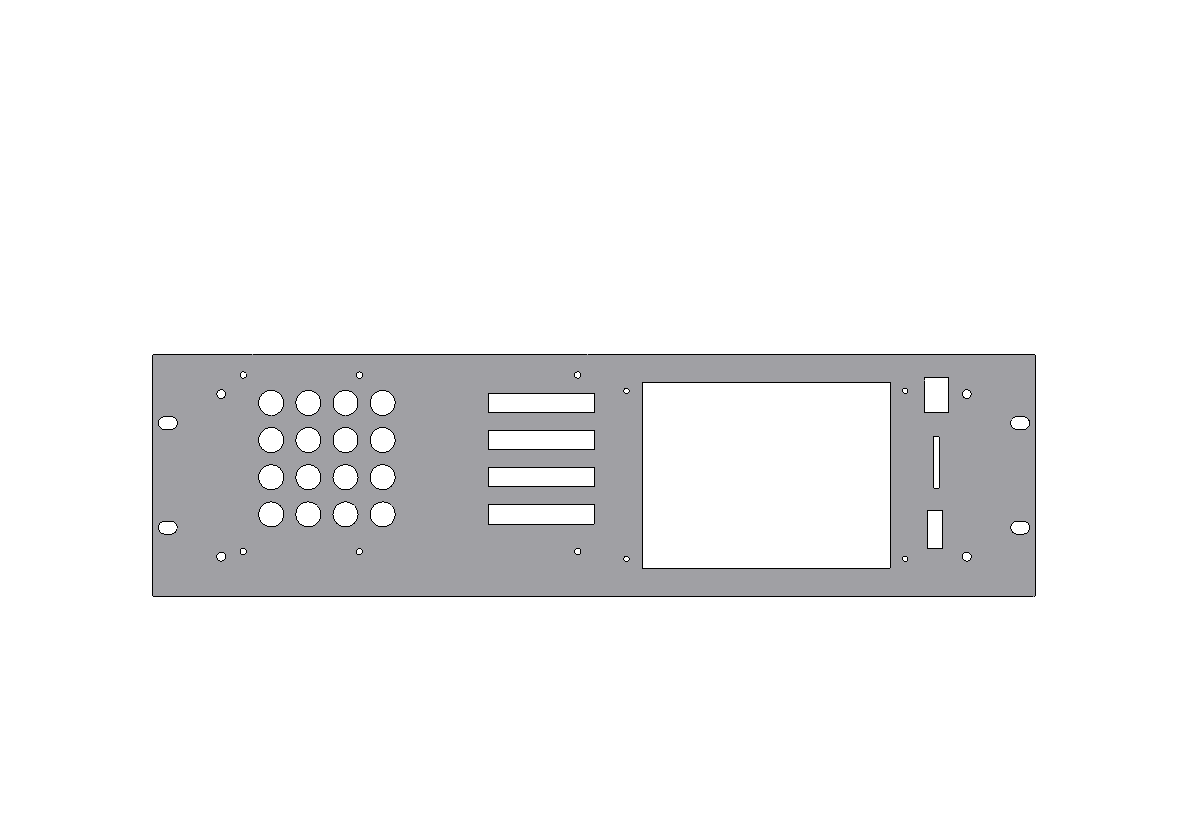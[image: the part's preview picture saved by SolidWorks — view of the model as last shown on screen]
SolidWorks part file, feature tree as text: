
SOLIDWORKS PART (.sldprt)
format: sldprt  version: not decoded by parser v0  size: 591,872 bytes
history: native  units: mm
features: sketch x11, cut_extrude x9, plane x4, sheet_metal_op x2, pattern_linear x2, material x1 + 2 further entries (+12 scaffold rows collapsed)
feature tree (43):
  "Annotations"  RD2=21.844mm RD1=3.4798mm
  scaffold x12  (default folders/planes/origin — collapsed)
  material  "Material <not specified>"
  sketch  "Sketch1"  dims[D3=1.016mm U Height=132.588mm Panel Std Width=482.6mm]
  sheet_metal_op  "Sheet-Metal1"  Thickness=1.905mm
  sheet_metal_op  "Front Panel"
  sketch  "Sketch2"  dims[c1.D1=6.35mm c1.D2=6.35mm c1.D3=3.175mm c2.D1=3.175mm c2.D4=3.175mm c2.D5=3.175mm c2.D7=3.175mm c2.D6=3.175mm c3.D1=3.175mm c3.D3=3.175mm c3.D4=3.175mm c3.D6=3.175mm c3.D7=3.175mm c3.D8=3.175mm c4.D1=3.175mm c4.Slot Radius=3.5433mm c4.D8=3.175mm c4.D10=3.175mm c4.D3=3.175mm c4.D4=3.175mm c4.D2=3.175mm c5.D3=6.35mm c5.D4=3.175mm c5.D5=82.1436mm c5.D6=90.0deg c5.D7=8.7376mm c6.D6=482.6mm c7.D6=90.0deg c8.D6=5.9944mm c8.D8=90.0deg c8.D9=8.7376mm c8.D10=5.9436mm c8.D11=465.1248mm c8.D3=25.4mm c9.D6=88.9mm c9.D3=127.0mm c9.D1=25.4mm c9.D2=8.7376mm c10.D3=144.78mm c10.D4=3.175mm c10.D5=16.51mm c10.D6=3.175mm c10.D7=10.3251mm c10.D8=16.51mm c11.D6=7.1501mm c11.D1=144.78mm c12.D1=90.0deg c12.D4=~8.58827mm c13.D1=144.78mm c14.D1=90.0deg c14.D2=7.1501mm c14.D4=3.175mm c15.D1=3.175mm c15.D3=144.78mm c15.D4=465.1248mm c15.D6=144.78mm c16.D6=90.0deg c17.D6=472.2749mm c17.D1=7.1501mm c18.D6=10.3251mm c18.D7=175.768mm c19.D7=90.0deg c20.D7=~7.099516mm c20.D8=7.1501mm c20.D9=144.78mm c21.D9=90.0deg c22.D9=16.51mm c22.D4=465.1248mm c22.Slot Movement=3.175mm c22.D3=16.51mm c23.D4=7.1501mm c23.D5=3.175mm c23.D6=6.35mm c24.D5=6.35mm c24.D6=90.0deg c24.D7=144.78mm c25.D7=90.0deg c26.D7=19.685mm c26.D8=144.78mm c26.D9=465.1248mm c26.D10=16.51mm c27.D7=7.1501mm c27.D8=16.51mm c27.D9=7.1501mm c27.D10=465.1248mm c27.Rack Mount Vertical Slot Location=28.575mm c27.Rack Mount Slot Ø=6.35mm c27.Rack Mount Slot Center Horizontal Location=233.0704mm c27.D1=0.0mm c27.D2=38.1mm c27.D3=95.25mm c28.D1=37.6936mm c28.D2=95.6564mm c29.D1=28.6004mm c29.D2=38.4556mm c29.D3=37.6936mm c30.D2=482.6mm c30.D1=37.6936mm c31.D2=10.287mm c31.D3=94.8944mm c31.D1=28.6004mm c32.D3=13.3858mm c32.D4=37.6936mm]
  sketch  "Sketch5"  dims[c1.D1=4.8514mm c1.D5=4.699mm c1.8-32 Clear. Holes=4.8514mm c1.D2=37.465mm c1.D3=407.67mm c1.D4=44.45mm c2.D5=88.9mm c2.D3=407.67mm c2.Panel Mounts Horizontal Location=203.835mm c2.Panel Mounts Vertical Location=44.45mm c2.D1=41.751mm]
  cut_extrude  "Front Panel Mounting Holes"  [1 undecoded]
  cut_extrude  "Rack Mounting Slot"  [1 undecoded]
  "Flat-Pattern1"
  sketch  "Bend-Lines1"
  sketch  "ADio mounting holes"  dims[c1.D1=3.4798mm c1.D2=3.4798mm c1.D3=3.4798mm c1.D4=3.4798mm c2.D2=3.4798mm c2.D3=3.4798mm c2.D4=3.4798mm c2.D5=3.4798mm c2.D6=3.4798mm c3.D5=184.15mm c3.D6=83.82mm c3.D7=50.8mm c3.D8=12.7mm c3.D2=12.7mm c3.D9=107.95mm c3.D10=69.85mm c3.D11=93.98mm]
  cut_extrude  "Cut-Extrude1"  Depth=2.54mm
  sketch  "Sketch8"  dims[c1.D1=13.716mm c1.D2=5.4102mm c1.D4=5.4102mm c2.D1=15.24mm c2.D2=12.7mm c3.D1=25.4mm c3.D2=22.86mm c3.D3=66.04mm c4.D2=15.24mm c4.D4=15.24mm c4.D3=15.24mm]
  cut_extrude  "BNC seed hole"  Depth=2.54mm
  pattern_linear  "BNC pattern"  Count1=4 Count2=4 Spacing1=20.32mm Spacing2=20.32mm
  sketch  "Sketch9"  dims[c1.D4=13.716mm c1.D1=1.5875mm c1.D2=1.5875mm c1.D3=1.5875mm c2.D4=1.5875mm c2.D5=0.1905mm c2.D1=10.668mm c2.D2=59.69mm c2.D3=5.334mm c3.D4=16.1925mm c3.D5=0.762mm c3.D2=0.762mm c3.D1=0.762mm c3.D3=0.762mm c4.D4=0.762mm]
  cut_extrude  "DIO Seed Hole"  Depth=2.54mm
  pattern_linear  "DIO Pattern"  Count1=4 Count2=1 Spacing1=20.32mm Spacing2=22.225mm
  sketch  "LCD view cutout"  dims[c1.D1=120.0mm c1.D2=90.0mm c1.D3=12.7mm c1.D4=82.55mm c2.D1=0.254mm c2.D2=0.254mm c2.D3=0.254mm c2.D4=0.254mm]
  cut_extrude  "LCD Cutout"  Depth=2.54mm
  sketch  "LCD mount holes"  dims[c1.D1=3.4798mm c1.D2=3.4798mm c1.D3=3.0mm c1.D4=3.4798mm c2.D1=3.0mm c2.D2=3.0mm c2.D4=3.0mm c2.D5=6.5mm c2.D6=101.0mm c2.D7=152.0mm c2.D8=22.0mm c2.D9=5.66mm c3.D8=22.0mm]
  cut_extrude  "LCD mount hole - cut"  Depth=2.54mm
  sketch  "Sketch10"  dims[D1=12.9mm D2=19.2mm D3=12.7mm D4=47.625mm]
  cut_extrude  "power sw - cut"  Depth=12.03mm
  sketch  "Sketch11"  dims[D1=0.0mm D2=0.254mm D3=0.254mm D4=0.254mm D5=0.254mm]
  cut_extrude  "Cut-Extrude8"  Depth=2.54mm
  plane  "LCD Center Plane YZ"  Offset=147.32mm
  plane  "LCD center Plane YX"  Offset=66.04mm
  plane  "ADIO left plane"  Offset=43.18mm
  plane  "ADIO top plane"  Offset=5.08mm
decode coverage: 20 of 24 modeling features carry decoded parameters; 2 rows unclassified (native names shown)
note: ~ marks probable driven/reference dimensions
note: 2 parameter values undecoded
note: suppression state not decoded; provenance and decode notes live in map.json
